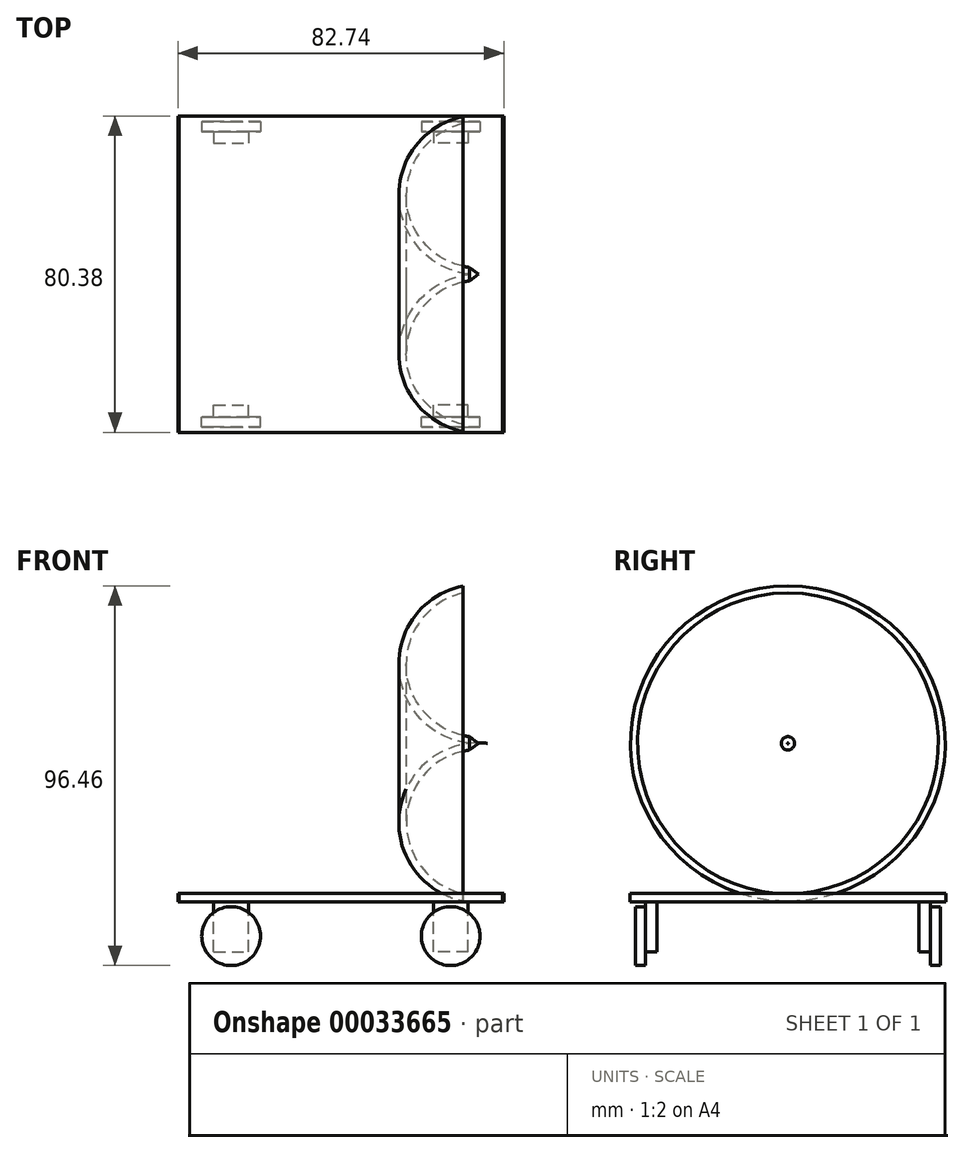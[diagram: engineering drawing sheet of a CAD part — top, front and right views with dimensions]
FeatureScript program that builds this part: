
annotation { "Feature Type Name" : "Feature", "Feature Type Description" : "" }
export const myFeature = defineFeature(function(context is Context, id is Id, definition is map)
    precondition{}
    {
        {
            var Q0;
            Q0=qCreatedBy(makeId("Front.planeOp"),FACE);
            var sketch = newSketch(context, id + "F0", { "sketchPlane" : qUnion([Q0])});
            skLineSegment(sketch, "E0.bottom", {"start": v(-41.1, 0) * mm, "end": v(41.37, 0) * mm});
            skLineSegment(sketch, "E0.top", {"start": v(-41.1, -2.18) * mm, "end": v(41.37, -2.18) * mm});
            skLineSegment(sketch, "E0.left", {"start": v(-41.1, 0) * mm, "end": v(-41.1, -2.18) * mm});
            skLineSegment(sketch, "E0.right", {"start": v(41.37, 0) * mm, "end": v(41.37, -2.18) * mm});
            skSolve(sketch);
        }
        {
            var Q0;
            Q0=makeQuery(id+"F0.imprint","IMPRINT",FACE,{"disambiguationData":[TD([[makeQuery(id+"F0.imprint","IMPRINT",EDGE,{"derivedFrom":sQuery(id+"F0.wireOp",EDGE,"E0.bottom")}),-1.0]])]});
            extrude(context, id + "F1", {"entities" : qUnion([Q0]), "endBound" : BoundingType.SYMMETRIC, "depth" : 80.37 * mm});
        }
        {
            var Q0;
            Q0=makeQuery(id+"F1.opExtrude","SWEPT_FACE",FACE,{"disambiguationData":[OSD([sQuery(id+"F0.wireOp",EDGE,"E0.top")])]});
            var sketch = newSketch(context, id + "F2", { "sketchPlane" : qUnion([Q0])});
            skLineSegment(sketch, "E1.bottom", {"start": v(-32.32, 36.25) * mm, "end": v(-23.47, 36.25) * mm});
            skLineSegment(sketch, "E1.top", {"start": v(-32.32, 33.3) * mm, "end": v(-23.47, 33.3) * mm});
            skLineSegment(sketch, "E1.left", {"start": v(-32.32, 36.25) * mm, "end": v(-32.32, 33.3) * mm});
            skLineSegment(sketch, "E1.right", {"start": v(-23.47, 36.25) * mm, "end": v(-23.47, 33.3) * mm});
            skSolve(sketch);
        }
        {
            var Q0;
            Q0=makeQuery(id+"F2.imprint","IMPRINT",FACE,{"disambiguationData":[TD([[makeQuery(id+"F2.imprint","IMPRINT",EDGE,{"derivedFrom":sQuery(id+"F2.wireOp",EDGE,"E1.bottom")}),-1.0]])]});
            extrude(context, id + "F3", {"entities" : qUnion([Q0]), "operationType" : NewBodyOperationType.ADD, "depth" : 12.7 * mm});
        }
        {
            var Q0;
            Q0=makeQuery(id+"F3.opExtrude","SWEPT_FACE",FACE,{"disambiguationData":[OSD([sQuery(id+"F2.wireOp",EDGE,"E1.bottom")])]});
            var sketch = newSketch(context, id + "F4", { "sketchPlane" : qUnion([Q0])});
            skCircle(sketch, "E2", {"center": v(-27.9, -10.89) * mm, "radius": 7.46 * mm});
            skPoint(sketch, "E2.centerSnap0", {"position": v(-27.9, -14.88) * mm});
            skSolve(sketch);
        }
        {
            var Q0;
            {var subQ0=sQuery(id+"F2.wireOp",EDGE,"E1.bottom");var subQ4=makeQuery(id+"F3.opExtrude","CAP_EDGE",EDGE,{"disambiguationData":[OSD([subQ0])],"isStart":false});Q0=makeQuery(id+"F4.imprint","IMPRINT",FACE,{"disambiguationData":[TD([[makeQuery(id+"F4.imprint","IMPRINT",EDGE,{"derivedFrom":subQ4}),-1.0]])]});}
            var Q1;
            {var subQ0=sQuery(id+"F2.wireOp",EDGE,"E1.bottom");var subQ4=makeQuery(id+"F3.opExtrude","CAP_EDGE",EDGE,{"disambiguationData":[OSD([subQ0])],"isStart":false});Q1=makeQuery(id+"F4.imprint","IMPRINT",FACE,{"disambiguationData":[TD([[makeQuery(id+"F4.imprint","IMPRINT",EDGE,{"derivedFrom":subQ4}),1.0]])]});}
            extrude(context, id + "F5", {"entities" : qUnion([Q0, Q1]), "operationType" : NewBodyOperationType.ADD, "depth" : 2.54 * mm});
        }
        {
            var Q0;
            Q0=makeQuery(id+"F1.opExtrude","SWEPT_BODY",BODY,{"disambiguationData":[OSD([sQuery(id+"F0.wireOp",EDGE,"E0.bottom"),sQuery(id+"F0.wireOp",EDGE,"E0.top"),sQuery(id+"F0.wireOp",EDGE,"E0.left"),sQuery(id+"F0.wireOp",EDGE,"E0.right")])]});
            var Q1;
            Q1=makeQuery(id+"F5.opExtrude","CAP_FACE",FACE,{"disambiguationData":[OSD([sQuery(id+"F4.wireOp",EDGE,"E2")])],"isStart":false});
            var Q2;
            Q2=makeQuery(id+"F5.opExtrude","SWEPT_FACE",FACE,{"disambiguationData":[OSD([sQuery(id+"F4.wireOp",EDGE,"E2")])]});
            var Q3;
            Q3=makeQuery(id+"F3.opExtrude","SWEPT_FACE",FACE,{"disambiguationData":[OSD([sQuery(id+"F2.wireOp",EDGE,"E1.right")])]});
            var Q4;
            Q4=makeQuery(id+"F5.opExtrude","CAP_FACE",FACE,{"disambiguationData":[OSD([sQuery(id+"F4.wireOp",EDGE,"E2")])],"isStart":true});
            var Q5;
            Q5=makeQuery(id+"F3.opExtrude","SWEPT_FACE",FACE,{"disambiguationData":[OSD([sQuery(id+"F2.wireOp",EDGE,"E1.top")])]});
            var Q6;
            Q6=makeQuery(id+"F3.opExtrude","SWEPT_FACE",FACE,{"disambiguationData":[OSD([sQuery(id+"F2.wireOp",EDGE,"E1.left")])]});
            var Q7;
            Q7=qCreatedBy(makeId("Right.planeOp"),FACE);
            mirror(context, id + "F6", {"entities" : qUnion([Q0]), "faces" : qUnion([Q1, Q2, Q3, Q4, Q5, Q6]), "mirrorPlane" : qUnion([Q7])});
        }
        {
            var Q0;
            Q0=makeQuery(id+"F6.opPattern","COPY",BODY,{"derivedFrom":makeQuery(id+"F1.opExtrude","SWEPT_BODY",BODY,{"disambiguationData":[OSD([sQuery(id+"F0.wireOp",EDGE,"E0.bottom"),sQuery(id+"F0.wireOp",EDGE,"E0.top"),sQuery(id+"F0.wireOp",EDGE,"E0.left"),sQuery(id+"F0.wireOp",EDGE,"E0.right")])]}),"instanceName":"1"});
            var Q1;
            Q1=makeQuery(id+"F1.opExtrude","SWEPT_BODY",BODY,{"disambiguationData":[OSD([sQuery(id+"F0.wireOp",EDGE,"E0.bottom"),sQuery(id+"F0.wireOp",EDGE,"E0.top"),sQuery(id+"F0.wireOp",EDGE,"E0.left"),sQuery(id+"F0.wireOp",EDGE,"E0.right")])]});
            var Q2;
            Q2=qCreatedBy(makeId("Front.planeOp"),FACE);
            mirror(context, id + "F7", {"entities" : qUnion([Q0, Q1]), "mirrorPlane" : qUnion([Q2])});
        }
        {
            var Q0;
            Q0=qCreatedBy(makeId("Top.planeOp"),FACE);
            cPlane(context, id + "F8", {"entities" : qUnion([Q0]), "cplaneType" : CPlaneType.OFFSET, "offset" : 38.1 * mm, "width" : 152.4 * mm, "height" : 152.4 * mm});
        }
        {
            var Q0;
            Q0=qCreatedBy(id+"F8.planeOp",FACE);
            var sketch = newSketch(context, id + "F9", { "sketchPlane" : qUnion([Q0])});
            skArc(sketch, "E3", {"start": v(31.02, 40) * mm, "mid": v(14.72, 19.3) * mm, "end": v(32.66, 0) * mm});
            skLineSegment(sketch, "E4", {"start": v(31.02, 40) * mm, "end": v(31.02, 38.21) * mm});
            skArc(sketch, "E5", {"start": v(31.02, 38.21) * mm, "mid": v(16.6, 19.28) * mm, "end": v(32.66, 1.7) * mm});
            skLineSegment(sketch, "E6", {"start": v(32.66, 1.7) * mm, "end": v(34.9, 0) * mm});
            skLineSegment(sketch, "E7", {"start": v(34.9, 0) * mm, "end": v(32.66, 0) * mm});
            skLineSegment(sketch, "E8", {"start": v(18.2, 0) * mm, "end": v(0, 0) * mm});
            skSolve(sketch);
        }
        {
            var Q0;
            Q0=makeQuery(id+"F9.imprint","IMPRINT",FACE,{"disambiguationData":[TD([[makeQuery(id+"F9.imprint","IMPRINT",EDGE,{"derivedFrom":sQuery(id+"F9.wireOp",EDGE,"E3")}),1.0]])]});
            var Q1;
            Q1=sQuery(id+"F9.wireOp",EDGE,"E8");
            revolve(context, id + "F10", {"entities" : qUnion([Q0]), "axis" : qUnion([Q1]), "revolveType" : RevolveType.FULL});
        }
    });
